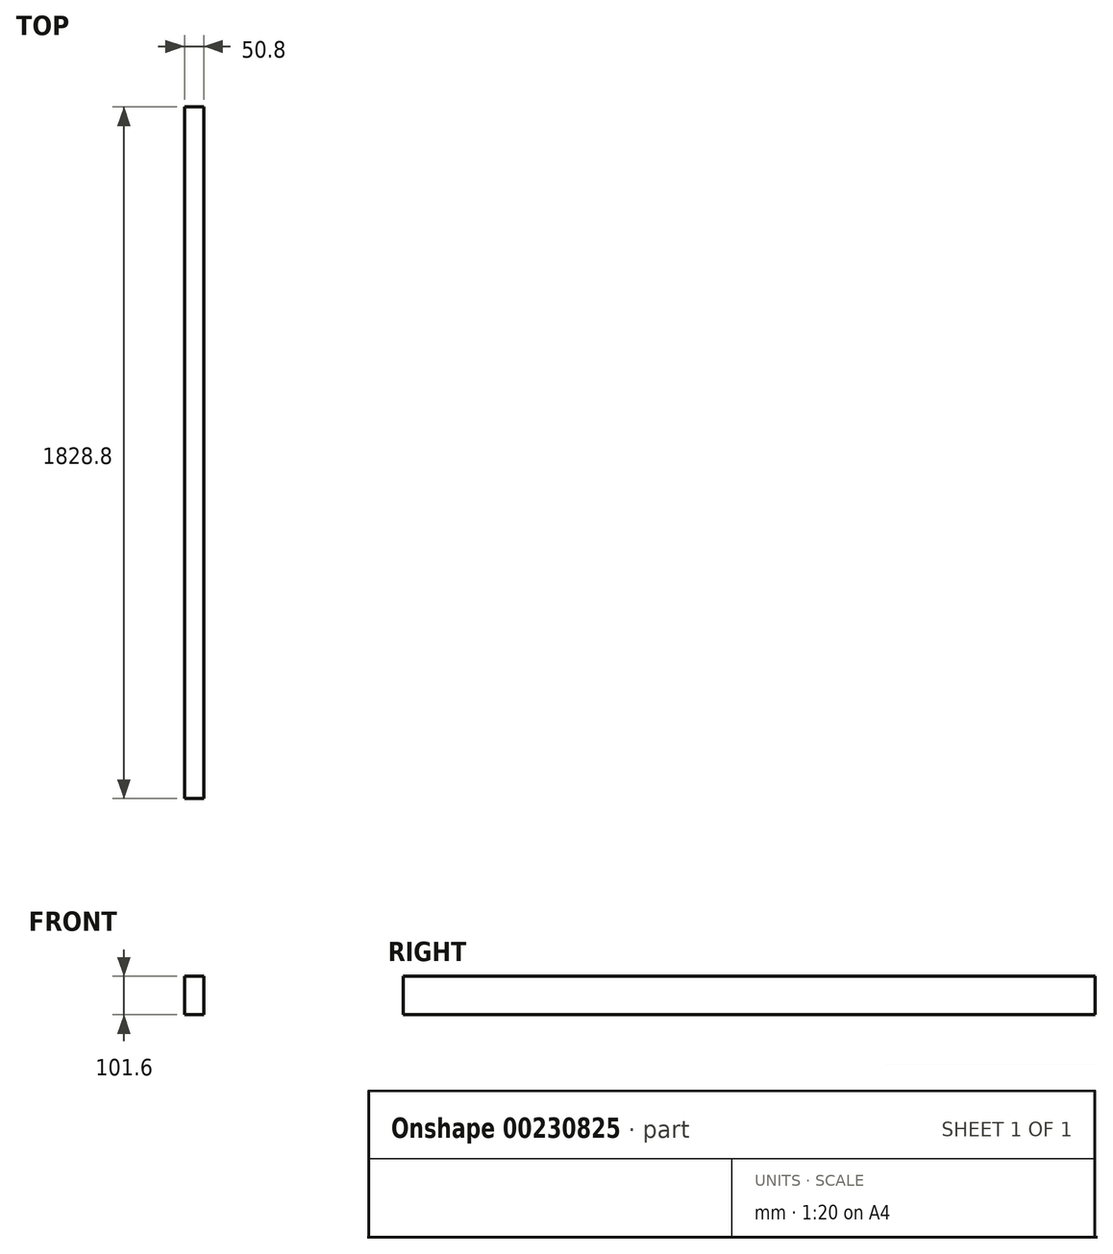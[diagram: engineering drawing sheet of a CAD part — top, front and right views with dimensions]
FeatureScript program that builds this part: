
annotation { "Feature Type Name" : "Feature", "Feature Type Description" : "" }
export const myFeature = defineFeature(function(context is Context, id is Id, definition is map)
    precondition{}
    {
        {
            var Q0;
            Q0=qCreatedBy(makeId("Top.planeOp"),FACE);
            var sketch = newSketch(context, id + "F0", { "sketchPlane" : qUnion([Q0])});
            skLineSegment(sketch, "E0.bottom", {"start": v(-69.1, 1574.44) * mm, "end": v(-18.3, 1574.44) * mm});
            skLineSegment(sketch, "E0.top", {"start": v(-69.1, -254.36) * mm, "end": v(-18.3, -254.36) * mm});
            skLineSegment(sketch, "E0.left", {"start": v(-69.1, 1574.44) * mm, "end": v(-69.1, -254.36) * mm});
            skLineSegment(sketch, "E0.right", {"start": v(-18.3, 1574.44) * mm, "end": v(-18.3, -254.36) * mm});
            skSolve(sketch);
        }
        {
            var Q0;
            Q0=makeQuery(id+"F0.imprint","IMPRINT",FACE,{"disambiguationData":[TD([[makeQuery(id+"F0.imprint","IMPRINT",EDGE,{"derivedFrom":sQuery(id+"F0.wireOp",EDGE,"E0.bottom")}),-1.0]])]});
            extrude(context, id + "F1", {"entities" : qUnion([Q0]), "depth" : 101.6 * mm});
        }
    });
